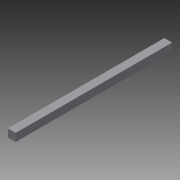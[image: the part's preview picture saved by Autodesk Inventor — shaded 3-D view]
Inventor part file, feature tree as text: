
AUTODESK INVENTOR PART (.ipt)
format: ipt  version: 2015 (Build 190159000, 159)  size: 67,584 bytes
history: native  units: in
note: dims shown in document units (in); Inventor stores cm internally (conversion verified against a paired STEP export)
features: extrude x1, sketch x1
ambient origin geometry x8: Origin, YZ Plane, XZ Plane, XY Plane, X Axis, Y Axis, Z Axis, Center Point
bodies: Solid1 (feature_tree)
feature tree (2):
  extrude  "Extrusion1"  Depth=0.75in
  sketch  "Sketch1"  dims[d0=0.75in d1=0.75in d2=15.0in d3=0.0in]
